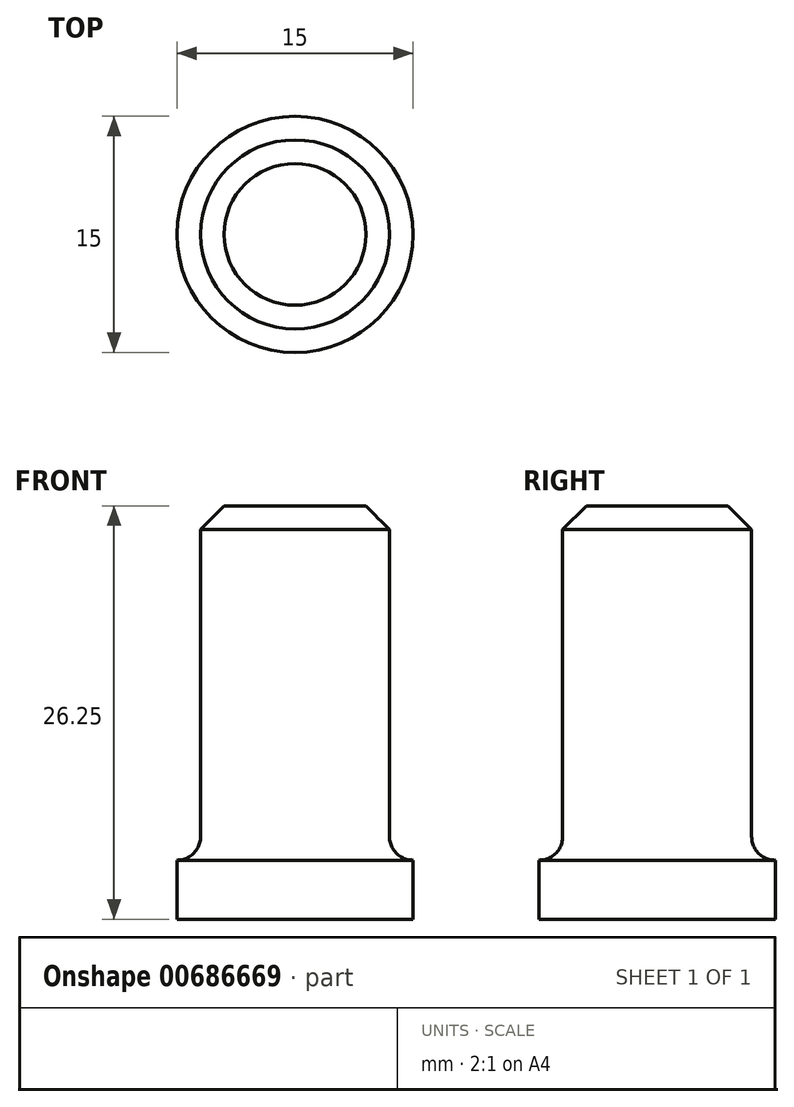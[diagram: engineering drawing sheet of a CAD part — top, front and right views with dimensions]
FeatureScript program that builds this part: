
annotation { "Feature Type Name" : "Feature", "Feature Type Description" : "" }
export const myFeature = defineFeature(function(context is Context, id is Id, definition is map)
    precondition{}
    {
        {
            var Q0;
            Q0=qCreatedBy(makeId("Front.planeOp"),FACE);
            var sketch = newSketch(context, id + "F0", { "sketchPlane" : qUnion([Q0])});
            skLineSegment(sketch, "E0.bottom", {"start": v(0, 0) * mm, "end": v(6, 0) * mm});
            skLineSegment(sketch, "E0.top", {"start": v(0, 22.5) * mm, "end": v(6, 22.5) * mm});
            skLineSegment(sketch, "E0.left", {"start": v(0, 0) * mm, "end": v(0, 22.5) * mm});
            skLineSegment(sketch, "E0.right", {"start": v(6, 0) * mm, "end": v(6, 22.5) * mm});
            skLineSegment(sketch, "E1.bottom", {"start": v(0, 0) * mm, "end": v(7.5, 0) * mm});
            skLineSegment(sketch, "E1.top", {"start": v(0, -3.75) * mm, "end": v(7.5, -3.75) * mm});
            skLineSegment(sketch, "E1.left", {"start": v(0, 0) * mm, "end": v(0, -3.75) * mm});
            skLineSegment(sketch, "E1.right", {"start": v(7.5, 0) * mm, "end": v(7.5, -3.75) * mm});
            skLineSegment(sketch, "E2", {"start": v(0, 24.6) * mm, "end": v(0, -7.44) * mm, "construction": true});
            skPoint(sketch, "E3", {"position": v(6, -3.75) * mm});
            skSolve(sketch);
        }
        {
            var Q0;
            Q0=makeQuery(id+"F0.imprint","IMPRINT",FACE,{"disambiguationData":[TD([[makeQuery(id+"F0.imprint","IMPRINT",EDGE,{"derivedFrom":sQuery(id+"F0.wireOp",EDGE,"E0.top")}),-1.0]])]});
            var Q1;
            Q1=makeQuery(id+"F0.imprint","IMPRINT",FACE,{"disambiguationData":[TD([[makeQuery(id+"F0.imprint","IMPRINT",EDGE,{"derivedFrom":sQuery(id+"F0.wireOp",EDGE,"E1.top")}),1.0]])]});
            var Q2;
            Q2=sQuery(id+"F0.wireOp",EDGE,"E2");
            revolve(context, id + "F1", {"entities" : qUnion([Q0, Q1]), "axis" : qUnion([Q2]), "revolveType" : RevolveType.FULL});
        }
        {
            var Q0;
            Q0=makeQuery(id+"F1.opRevolve","SWEPT_EDGE",EDGE,{"disambiguationData":[OSD([sQuery(id+"F0.wireOp",EDGE,"E0.top"),sQuery(id+"F0.wireOp",EDGE,"E0.right")])]});
            chamfer(context, id + "F2", {"entities" : qUnion([Q0]), "width" : 1.5 * mm, "tangentPropagation" : true});
        }
        {
            var Q0;
            Q0=makeQuery(id+"F1.opRevolve","SWEPT_EDGE",EDGE,{"disambiguationData":[OSD([sQuery(id+"F0.wireOp",EDGE,"E0.right"),sQuery(id+"F0.wireOp",EDGE,"E1.bottom")])]});
            fillet(context, id + "F3", {"entities" : qUnion([Q0]), "radius" : 1.5 * mm, "tangentPropagation" : true, "allowEdgeOverflow" : false});
        }
    });
